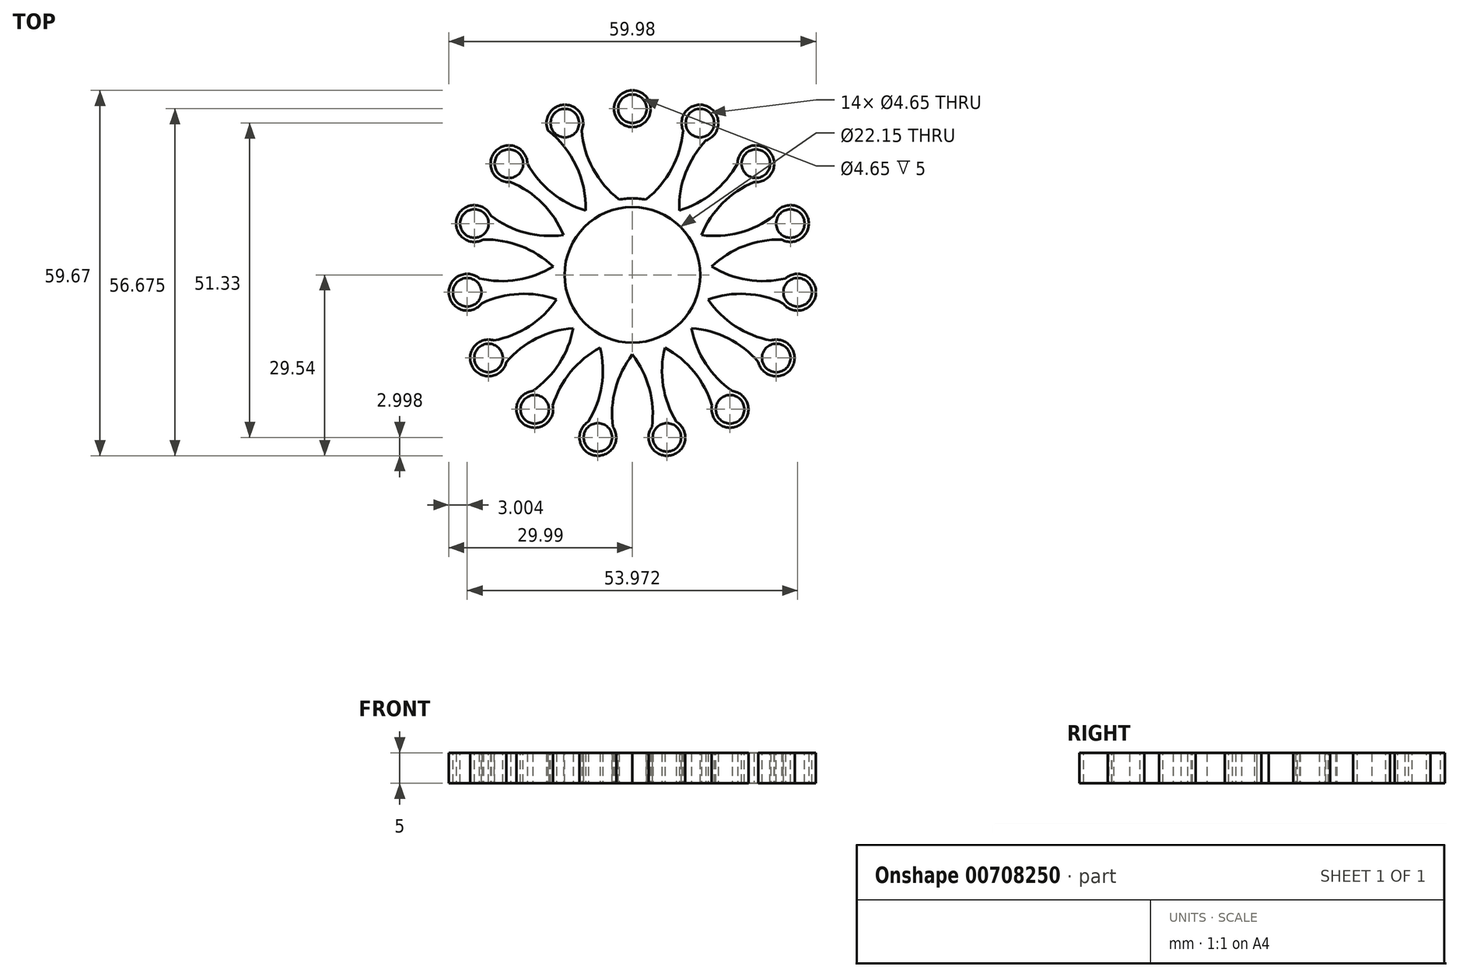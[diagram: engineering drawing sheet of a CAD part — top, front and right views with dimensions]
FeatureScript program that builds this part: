
annotation { "Feature Type Name" : "Feature", "Feature Type Description" : "" }
export const myFeature = defineFeature(function(context is Context, id is Id, definition is map)
    precondition{}
    {
        {
            var Q0;
            Q0=qCreatedBy(makeId("Top.planeOp"),FACE);
            var sketch = newSketch(context, id + "F0", { "sketchPlane" : qUnion([Q0])});
            skCircle(sketch, "E0", {"center": v(0, 0) * mm, "radius": 12.5 * mm});
            skCircle(sketch, "E1", {"center": v(0, 27.13) * mm, "radius": 3 * mm});
            skLineSegment(sketch, "E2", {"start": v(-3, 12.13) * mm, "end": v(3, 12.13) * mm});
            skArc(sketch, "E3", {"start": v(-3, 12.13) * mm, "mid": v(-1.13, 19.63) * mm, "end": v(-3, 27.13) * mm});
            skArc(sketch, "E4", {"start": v(3, 27.13) * mm, "mid": v(1.13, 19.63) * mm, "end": v(3, 12.13) * mm});
            skArc(sketch, "E5.1.0", {"start": v(-8.3, 26) * mm, "mid": v(-6.95, 18.4) * mm, "end": v(-2.2, 12.3) * mm});
            skArc(sketch, "E5.1.2", {"start": v(-7.68, 9.87) * mm, "mid": v(-9.02, 17.48) * mm, "end": v(-13.78, 23.57) * mm});
            skCircle(sketch, "E5.1.3", {"center": v(-11.04, 24.79) * mm, "radius": 3 * mm});
            skLineSegment(sketch, "E5.1.4", {"start": v(-7.68, 9.87) * mm, "end": v(-2.2, 12.3) * mm});
            skArc(sketch, "E5.2.0", {"start": v(-18.16, 20.39) * mm, "mid": v(-13.83, 13.98) * mm, "end": v(-7.01, 10.35) * mm});
            skArc(sketch, "E5.2.2", {"start": v(-11.03, 5.9) * mm, "mid": v(-15.35, 12.3) * mm, "end": v(-22.17, 15.93) * mm});
            skCircle(sketch, "E5.2.3", {"center": v(-20.16, 18.16) * mm, "radius": 3 * mm});
            skLineSegment(sketch, "E5.2.4", {"start": v(-11.03, 5.9) * mm, "end": v(-7.01, 10.35) * mm});
            skArc(sketch, "E6.6.3.0", {"start": v(-12.47, 0.9) * mm, "mid": v(-19.02, 4.99) * mm, "end": v(-26.73, 5.53) * mm});
            skArc(sketch, "E6.7.3.0", {"start": v(-24.88, 11.24) * mm, "mid": v(-18.32, 7.15) * mm, "end": v(-10.61, 6.6) * mm});
            skCircle(sketch, "E6.10.3.0", {"center": v(-25.8, 8.39) * mm, "radius": 3 * mm});
            skLineSegment(sketch, "E6.12.3.0", {"start": v(-12.47, 0.9) * mm, "end": v(-10.61, 6.6) * mm});
            skArc(sketch, "E6.6.4.0", {"start": v(-11.75, -4.25) * mm, "mid": v(-19.4, -3.18) * mm, "end": v(-26.67, -5.82) * mm});
            skArc(sketch, "E6.7.4.0", {"start": v(-27.3, 0.15) * mm, "mid": v(-19.65, -0.93) * mm, "end": v(-12.38, 1.72) * mm});
            skCircle(sketch, "E6.10.4.0", {"center": v(-26.99, -2.84) * mm, "radius": 3 * mm});
            skLineSegment(sketch, "E6.12.4.0", {"start": v(-11.75, -4.25) * mm, "end": v(-12.38, 1.72) * mm});
            skArc(sketch, "E6.6.5.0", {"start": v(-9, -8.67) * mm, "mid": v(-16.44, -10.8) * mm, "end": v(-22, -16.17) * mm});
            skArc(sketch, "E6.7.5.0", {"start": v(-25, -10.97) * mm, "mid": v(-17.57, -8.84) * mm, "end": v(-12, -3.47) * mm});
            skCircle(sketch, "E6.10.5.0", {"center": v(-23.5, -13.57) * mm, "radius": 3 * mm});
            skLineSegment(sketch, "E6.12.5.0", {"start": v(-9, -8.67) * mm, "end": v(-12, -3.47) * mm});
            skArc(sketch, "E6.6.6.0", {"start": v(-4.7, -11.58) * mm, "mid": v(-10.62, -16.55) * mm, "end": v(-13.52, -23.72) * mm});
            skArc(sketch, "E6.7.6.0", {"start": v(-18.38, -20.19) * mm, "mid": v(-12.46, -15.22) * mm, "end": v(-9.56, -8.05) * mm});
            skCircle(sketch, "E6.10.6.0", {"center": v(-15.95, -21.95) * mm, "radius": 3 * mm});
            skLineSegment(sketch, "E6.12.6.0", {"start": v(-4.7, -11.58) * mm, "end": v(-9.56, -8.05) * mm});
            skArc(sketch, "E7.6.7.0", {"start": v(0.41, -12.5) * mm, "mid": v(-2.97, -19.44) * mm, "end": v(-2.7, -27.17) * mm});
            skArc(sketch, "E7.7.7.0", {"start": v(-8.58, -25.92) * mm, "mid": v(-5.2, -18.97) * mm, "end": v(-5.46, -11.25) * mm});
            skCircle(sketch, "E7.10.7.0", {"center": v(-5.64, -26.54) * mm, "radius": 3 * mm});
            skLineSegment(sketch, "E7.12.7.0", {"start": v(0.41, -12.5) * mm, "end": v(-5.46, -11.25) * mm});
            skArc(sketch, "E7.6.8.0", {"start": v(5.46, -11.25) * mm, "mid": v(5.2, -18.97) * mm, "end": v(8.58, -25.92) * mm});
            skArc(sketch, "E7.7.8.0", {"start": v(2.7, -27.17) * mm, "mid": v(2.97, -19.44) * mm, "end": v(-0.41, -12.5) * mm});
            skCircle(sketch, "E7.10.8.0", {"center": v(5.64, -26.54) * mm, "radius": 3 * mm});
            skLineSegment(sketch, "E7.12.8.0", {"start": v(5.46, -11.25) * mm, "end": v(-0.41, -12.5) * mm});
            skArc(sketch, "E7.6.9.0", {"start": v(9.56, -8.05) * mm, "mid": v(12.46, -15.22) * mm, "end": v(18.38, -20.19) * mm});
            skArc(sketch, "E7.7.9.0", {"start": v(13.52, -23.72) * mm, "mid": v(10.62, -16.55) * mm, "end": v(4.7, -11.58) * mm});
            skCircle(sketch, "E7.10.9.0", {"center": v(15.95, -21.95) * mm, "radius": 3 * mm});
            skLineSegment(sketch, "E7.12.9.0", {"start": v(9.56, -8.05) * mm, "end": v(4.7, -11.58) * mm});
            skArc(sketch, "E7.6.10.0", {"start": v(12, -3.47) * mm, "mid": v(17.57, -8.84) * mm, "end": v(25, -10.97) * mm});
            skArc(sketch, "E7.7.10.0", {"start": v(22, -16.17) * mm, "mid": v(16.44, -10.8) * mm, "end": v(9, -8.67) * mm});
            skCircle(sketch, "E7.10.10.0", {"center": v(23.5, -13.57) * mm, "radius": 3 * mm});
            skLineSegment(sketch, "E7.12.10.0", {"start": v(12, -3.47) * mm, "end": v(9, -8.67) * mm});
            skArc(sketch, "E7.6.11.0", {"start": v(12.38, 1.72) * mm, "mid": v(19.65, -0.93) * mm, "end": v(27.3, 0.15) * mm});
            skArc(sketch, "E7.7.11.0", {"start": v(26.67, -5.82) * mm, "mid": v(19.4, -3.18) * mm, "end": v(11.75, -4.25) * mm});
            skCircle(sketch, "E7.10.11.0", {"center": v(26.99, -2.84) * mm, "radius": 3 * mm});
            skLineSegment(sketch, "E7.12.11.0", {"start": v(12.38, 1.72) * mm, "end": v(11.75, -4.25) * mm});
            skArc(sketch, "E7.6.12.0", {"start": v(10.61, 6.6) * mm, "mid": v(18.32, 7.15) * mm, "end": v(24.88, 11.24) * mm});
            skArc(sketch, "E7.7.12.0", {"start": v(26.73, 5.53) * mm, "mid": v(19.02, 4.99) * mm, "end": v(12.47, 0.9) * mm});
            skCircle(sketch, "E7.10.12.0", {"center": v(25.8, 8.39) * mm, "radius": 3 * mm});
            skLineSegment(sketch, "E7.12.12.0", {"start": v(10.61, 6.6) * mm, "end": v(12.47, 0.9) * mm});
            skArc(sketch, "E7.6.13.0", {"start": v(7.01, 10.35) * mm, "mid": v(13.83, 13.98) * mm, "end": v(18.16, 20.39) * mm});
            skArc(sketch, "E7.7.13.0", {"start": v(22.17, 15.93) * mm, "mid": v(15.35, 12.3) * mm, "end": v(11.03, 5.9) * mm});
            skCircle(sketch, "E7.10.13.0", {"center": v(20.16, 18.16) * mm, "radius": 3 * mm});
            skLineSegment(sketch, "E7.12.13.0", {"start": v(7.01, 10.35) * mm, "end": v(11.03, 5.9) * mm});
            skArc(sketch, "E7.6.14.0", {"start": v(2.2, 12.3) * mm, "mid": v(6.95, 18.4) * mm, "end": v(8.3, 26) * mm});
            skArc(sketch, "E7.7.14.0", {"start": v(13.78, 23.57) * mm, "mid": v(9.02, 17.48) * mm, "end": v(7.68, 9.87) * mm});
            skCircle(sketch, "E7.10.14.0", {"center": v(11.04, 24.79) * mm, "radius": 3 * mm});
            skLineSegment(sketch, "E7.12.14.0", {"start": v(2.2, 12.3) * mm, "end": v(7.68, 9.87) * mm});
            skSolve(sketch);
        }
        {
            var Q0;
            {var subQ0=sQuery(id+"F0.wireOp",EDGE,"E7.6.14.0");var subQ1=sQuery(id+"F0.wireOp",EDGE,"E4");var subQ2=makeQuery(id+"F0.imprint","INTERSECT",VERTEX,{"derivedFrom":[subQ1,subQ0]});Q0=makeQuery(id+"F0.imprint","IMPRINT",FACE,{"disambiguationData":[TD([[makeQuery(id+"F0.imprint","IMPRINT",EDGE,{"disambiguationData":[TD([[subQ2,-1.0]])],"derivedFrom":subQ0}),-1.0]])]});}
            var Q1;
            {var subQ0=sQuery(id+"F0.wireOp",EDGE,"E6.10.5.0");var subQ1=sQuery(id+"F0.wireOp",EDGE,"E6.6.5.0");var subQ2=makeQuery(id+"F0.imprint","INTERSECT",VERTEX,{"disambiguationData":[OD(0.0)],"derivedFrom":[subQ1,subQ0]});Q1=makeQuery(id+"F0.imprint","IMPRINT",FACE,{"disambiguationData":[TD([[makeQuery(id+"F0.imprint","IMPRINT",EDGE,{"disambiguationData":[TD([[subQ2,1.0]])],"derivedFrom":subQ1}),-1.0]])]});}
            var Q2;
            {var subQ1=sQuery(id+"F0.wireOp",EDGE,"E6.6.6.0");var subQ9=sQuery(id+"F0.wireOp",EDGE,"E7.7.7.0");var subQ11=makeQuery(id+"F0.imprint","INTERSECT",VERTEX,{"derivedFrom":[subQ1,subQ9]});Q2=makeQuery(id+"F0.imprint","IMPRINT",FACE,{"disambiguationData":[TD([[makeQuery(id+"F0.imprint","IMPRINT",EDGE,{"disambiguationData":[TD([[subQ11,-1.0]])],"derivedFrom":subQ1}),-1.0]])]});}
            var Q3;
            {var subQ0=sQuery(id+"F0.wireOp",EDGE,"E5.2.3");var subQ1=sQuery(id+"F0.wireOp",EDGE,"E5.2.0");var subQ2=makeQuery(id+"F0.imprint","INTERSECT",VERTEX,{"disambiguationData":[OD(0.0)],"derivedFrom":[subQ1,subQ0]});Q3=makeQuery(id+"F0.imprint","IMPRINT",FACE,{"disambiguationData":[TD([[makeQuery(id+"F0.imprint","IMPRINT",EDGE,{"disambiguationData":[TD([[subQ2,-1.0]])],"derivedFrom":subQ1}),-1.0]])]});}
            var Q4;
            {var subQ0=sQuery(id+"F0.wireOp",EDGE,"E7.10.8.0");var subQ1=sQuery(id+"F0.wireOp",EDGE,"E7.6.8.0");var subQ2=makeQuery(id+"F0.imprint","INTERSECT",VERTEX,{"disambiguationData":[OD(0.0)],"derivedFrom":[subQ1,subQ0]});Q4=makeQuery(id+"F0.imprint","IMPRINT",FACE,{"disambiguationData":[TD([[makeQuery(id+"F0.imprint","IMPRINT",EDGE,{"disambiguationData":[TD([[subQ2,1.0]])],"derivedFrom":subQ1}),-1.0]])]});}
            var Q5;
            {var subQ1=sQuery(id+"F0.wireOp",EDGE,"E7.6.10.0");var subQ9=sQuery(id+"F0.wireOp",EDGE,"E7.7.11.0");var subQ11=makeQuery(id+"F0.imprint","INTERSECT",VERTEX,{"derivedFrom":[subQ1,subQ9]});Q5=makeQuery(id+"F0.imprint","IMPRINT",FACE,{"disambiguationData":[TD([[makeQuery(id+"F0.imprint","IMPRINT",EDGE,{"disambiguationData":[TD([[subQ11,-1.0]])],"derivedFrom":subQ1}),-1.0]])]});}
            var Q6;
            {var subQ0=sQuery(id+"F0.wireOp",EDGE,"E5.1.3");var subQ1=sQuery(id+"F0.wireOp",EDGE,"E5.1.0");var subQ2=makeQuery(id+"F0.imprint","INTERSECT",VERTEX,{"disambiguationData":[OD(0.0)],"derivedFrom":[subQ1,subQ0]});Q6=makeQuery(id+"F0.imprint","IMPRINT",FACE,{"disambiguationData":[TD([[makeQuery(id+"F0.imprint","IMPRINT",EDGE,{"disambiguationData":[TD([[subQ2,-1.0]])],"derivedFrom":subQ1}),-1.0]])]});}
            var Q7;
            {var subQ1=sQuery(id+"F0.wireOp",EDGE,"E7.6.9.0");var subQ9=sQuery(id+"F0.wireOp",EDGE,"E7.7.10.0");var subQ11=makeQuery(id+"F0.imprint","INTERSECT",VERTEX,{"derivedFrom":[subQ1,subQ9]});Q7=makeQuery(id+"F0.imprint","IMPRINT",FACE,{"disambiguationData":[TD([[makeQuery(id+"F0.imprint","IMPRINT",EDGE,{"disambiguationData":[TD([[subQ11,-1.0]])],"derivedFrom":subQ1}),-1.0]])]});}
            var Q8;
            {var subQ0=sQuery(id+"F0.wireOp",EDGE,"E7.10.12.0");var subQ1=sQuery(id+"F0.wireOp",EDGE,"E7.6.12.0");var subQ2=makeQuery(id+"F0.imprint","INTERSECT",VERTEX,{"disambiguationData":[OD(0.0)],"derivedFrom":[subQ1,subQ0]});Q8=makeQuery(id+"F0.imprint","IMPRINT",FACE,{"disambiguationData":[TD([[makeQuery(id+"F0.imprint","IMPRINT",EDGE,{"disambiguationData":[TD([[subQ2,1.0]])],"derivedFrom":subQ1}),-1.0]])]});}
            var Q9;
            {var subQ1=sQuery(id+"F0.wireOp",EDGE,"E7.6.12.0");var subQ7=sQuery(id+"F0.wireOp",EDGE,"E7.7.13.0");var subQ8=makeQuery(id+"F0.imprint","INTERSECT",VERTEX,{"derivedFrom":[subQ1,subQ7]});Q9=makeQuery(id+"F0.imprint","IMPRINT",FACE,{"disambiguationData":[TD([[makeQuery(id+"F0.imprint","IMPRINT",EDGE,{"disambiguationData":[TD([[subQ8,-1.0]])],"derivedFrom":subQ1}),-1.0]])]});}
            var Q10;
            {var subQ1=sQuery(id+"F0.wireOp",EDGE,"E7.6.7.0");var subQ9=sQuery(id+"F0.wireOp",EDGE,"E7.7.8.0");var subQ11=makeQuery(id+"F0.imprint","INTERSECT",VERTEX,{"derivedFrom":[subQ1,subQ9]});Q10=makeQuery(id+"F0.imprint","IMPRINT",FACE,{"disambiguationData":[TD([[makeQuery(id+"F0.imprint","IMPRINT",EDGE,{"disambiguationData":[TD([[subQ11,-1.0]])],"derivedFrom":subQ1}),-1.0]])]});}
            var Q11;
            {var subQ0=sQuery(id+"F0.wireOp",EDGE,"E6.10.6.0");var subQ1=sQuery(id+"F0.wireOp",EDGE,"E6.6.6.0");var subQ2=makeQuery(id+"F0.imprint","INTERSECT",VERTEX,{"disambiguationData":[OD(0.0)],"derivedFrom":[subQ1,subQ0]});Q11=makeQuery(id+"F0.imprint","IMPRINT",FACE,{"disambiguationData":[TD([[makeQuery(id+"F0.imprint","IMPRINT",EDGE,{"disambiguationData":[TD([[subQ2,1.0]])],"derivedFrom":subQ1}),-1.0]])]});}
            var Q12;
            {var subQ1=sQuery(id+"F0.wireOp",EDGE,"E6.6.4.0");var subQ9=sQuery(id+"F0.wireOp",EDGE,"E6.7.5.0");var subQ11=makeQuery(id+"F0.imprint","INTERSECT",VERTEX,{"derivedFrom":[subQ1,subQ9]});Q12=makeQuery(id+"F0.imprint","IMPRINT",FACE,{"disambiguationData":[TD([[makeQuery(id+"F0.imprint","IMPRINT",EDGE,{"disambiguationData":[TD([[subQ11,-1.0]])],"derivedFrom":subQ1}),-1.0]])]});}
            var Q13;
            {var subQ1=sQuery(id+"F0.wireOp",EDGE,"E5.2.0");var subQ8=sQuery(id+"F0.wireOp",EDGE,"E5.1.2");var subQ11=makeQuery(id+"F0.imprint","INTERSECT",VERTEX,{"derivedFrom":[subQ8,subQ1]});Q13=makeQuery(id+"F0.imprint","IMPRINT",FACE,{"disambiguationData":[TD([[makeQuery(id+"F0.imprint","IMPRINT",EDGE,{"disambiguationData":[TD([[subQ11,1.0]])],"derivedFrom":subQ1}),-1.0]])]});}
            var Q14;
            {var subQ15=sQuery(id+"F0.wireOp",EDGE,"E5.1.4");var subQ16=sQuery(id+"F0.wireOp",EDGE,"E2");var subQ17=makeQuery(id+"F0.imprint","INTERSECT",VERTEX,{"derivedFrom":[subQ16,subQ15]});Q14=makeQuery(id+"F0.imprint","IMPRINT",FACE,{"disambiguationData":[TD([[makeQuery(id+"F0.imprint","IMPRINT",EDGE,{"disambiguationData":[TD([[subQ17,-1.0]])],"derivedFrom":subQ16}),-1.0]])]});}
            var Q15;
            {var subQ1=sQuery(id+"F0.wireOp",EDGE,"E6.6.5.0");var subQ9=sQuery(id+"F0.wireOp",EDGE,"E6.7.6.0");var subQ11=makeQuery(id+"F0.imprint","INTERSECT",VERTEX,{"derivedFrom":[subQ1,subQ9]});Q15=makeQuery(id+"F0.imprint","IMPRINT",FACE,{"disambiguationData":[TD([[makeQuery(id+"F0.imprint","IMPRINT",EDGE,{"disambiguationData":[TD([[subQ11,-1.0]])],"derivedFrom":subQ1}),-1.0]])]});}
            var Q16;
            {var subQ1=sQuery(id+"F0.wireOp",EDGE,"E7.6.13.0");var subQ7=sQuery(id+"F0.wireOp",EDGE,"E7.7.14.0");var subQ10=makeQuery(id+"F0.imprint","INTERSECT",VERTEX,{"derivedFrom":[subQ1,subQ7]});Q16=makeQuery(id+"F0.imprint","IMPRINT",FACE,{"disambiguationData":[TD([[makeQuery(id+"F0.imprint","IMPRINT",EDGE,{"disambiguationData":[TD([[subQ10,-1.0]])],"derivedFrom":subQ1}),-1.0]])]});}
            var Q17;
            {var subQ0=sQuery(id+"F0.wireOp",EDGE,"E7.10.14.0");var subQ1=sQuery(id+"F0.wireOp",EDGE,"E7.6.14.0");var subQ2=makeQuery(id+"F0.imprint","INTERSECT",VERTEX,{"disambiguationData":[OD(0.0)],"derivedFrom":[subQ1,subQ0]});Q17=makeQuery(id+"F0.imprint","IMPRINT",FACE,{"disambiguationData":[TD([[makeQuery(id+"F0.imprint","IMPRINT",EDGE,{"disambiguationData":[TD([[subQ2,1.0]])],"derivedFrom":subQ1}),-1.0]])]});}
            var Q18;
            {var subQ1=sQuery(id+"F0.wireOp",EDGE,"E7.6.8.0");var subQ9=sQuery(id+"F0.wireOp",EDGE,"E7.7.9.0");var subQ11=makeQuery(id+"F0.imprint","INTERSECT",VERTEX,{"derivedFrom":[subQ1,subQ9]});Q18=makeQuery(id+"F0.imprint","IMPRINT",FACE,{"disambiguationData":[TD([[makeQuery(id+"F0.imprint","IMPRINT",EDGE,{"disambiguationData":[TD([[subQ11,-1.0]])],"derivedFrom":subQ1}),-1.0]])]});}
            var Q19;
            {var subQ1=sQuery(id+"F0.wireOp",EDGE,"E7.6.11.0");var subQ7=sQuery(id+"F0.wireOp",EDGE,"E7.7.12.0");var subQ8=makeQuery(id+"F0.imprint","INTERSECT",VERTEX,{"derivedFrom":[subQ1,subQ7]});Q19=makeQuery(id+"F0.imprint","IMPRINT",FACE,{"disambiguationData":[TD([[makeQuery(id+"F0.imprint","IMPRINT",EDGE,{"disambiguationData":[TD([[subQ8,-1.0]])],"derivedFrom":subQ1}),-1.0]])]});}
            var Q20;
            {var subQ0=sQuery(id+"F0.wireOp",EDGE,"E3");var subQ1=sQuery(id+"F0.wireOp",EDGE,"E1");var subQ2=makeQuery(id+"F0.imprint","INTERSECT",VERTEX,{"disambiguationData":[OD(0.0)],"derivedFrom":[subQ1,subQ0]});Q20=makeQuery(id+"F0.imprint","IMPRINT",FACE,{"disambiguationData":[TD([[makeQuery(id+"F0.imprint","IMPRINT",EDGE,{"disambiguationData":[TD([[subQ2,1.0]])],"derivedFrom":subQ1}),1.0]])]});}
            var Q21;
            {var subQ0=sQuery(id+"F0.wireOp",EDGE,"E6.10.3.0");var subQ1=sQuery(id+"F0.wireOp",EDGE,"E6.6.3.0");var subQ2=makeQuery(id+"F0.imprint","INTERSECT",VERTEX,{"disambiguationData":[OD(0.0)],"derivedFrom":[subQ1,subQ0]});Q21=makeQuery(id+"F0.imprint","IMPRINT",FACE,{"disambiguationData":[TD([[makeQuery(id+"F0.imprint","IMPRINT",EDGE,{"disambiguationData":[TD([[subQ2,1.0]])],"derivedFrom":subQ1}),-1.0]])]});}
            var Q22;
            {var subQ0=sQuery(id+"F0.wireOp",EDGE,"E7.10.11.0");var subQ1=sQuery(id+"F0.wireOp",EDGE,"E7.6.11.0");var subQ2=makeQuery(id+"F0.imprint","INTERSECT",VERTEX,{"disambiguationData":[OD(0.0)],"derivedFrom":[subQ1,subQ0]});Q22=makeQuery(id+"F0.imprint","IMPRINT",FACE,{"disambiguationData":[TD([[makeQuery(id+"F0.imprint","IMPRINT",EDGE,{"disambiguationData":[TD([[subQ2,1.0]])],"derivedFrom":subQ1}),-1.0]])]});}
            var Q23;
            {var subQ0=sQuery(id+"F0.wireOp",EDGE,"E6.10.4.0");var subQ1=sQuery(id+"F0.wireOp",EDGE,"E6.6.4.0");var subQ2=makeQuery(id+"F0.imprint","INTERSECT",VERTEX,{"disambiguationData":[OD(0.0)],"derivedFrom":[subQ1,subQ0]});Q23=makeQuery(id+"F0.imprint","IMPRINT",FACE,{"disambiguationData":[TD([[makeQuery(id+"F0.imprint","IMPRINT",EDGE,{"disambiguationData":[TD([[subQ2,1.0]])],"derivedFrom":subQ1}),-1.0]])]});}
            var Q24;
            {var subQ3=sQuery(id+"F0.wireOp",EDGE,"E3");var subQ8=sQuery(id+"F0.wireOp",EDGE,"E1");var subQ11=makeQuery(id+"F0.imprint","INTERSECT",VERTEX,{"disambiguationData":[OD(1.0)],"derivedFrom":[subQ8,subQ3]});Q24=makeQuery(id+"F0.imprint","IMPRINT",FACE,{"disambiguationData":[TD([[makeQuery(id+"F0.imprint","IMPRINT",EDGE,{"disambiguationData":[TD([[subQ11,-1.0]])],"derivedFrom":subQ8}),-1.0]])]});}
            var Q25;
            {var subQ0=sQuery(id+"F0.wireOp",EDGE,"E7.10.9.0");var subQ1=sQuery(id+"F0.wireOp",EDGE,"E7.6.9.0");var subQ2=makeQuery(id+"F0.imprint","INTERSECT",VERTEX,{"disambiguationData":[OD(0.0)],"derivedFrom":[subQ1,subQ0]});Q25=makeQuery(id+"F0.imprint","IMPRINT",FACE,{"disambiguationData":[TD([[makeQuery(id+"F0.imprint","IMPRINT",EDGE,{"disambiguationData":[TD([[subQ2,1.0]])],"derivedFrom":subQ1}),-1.0]])]});}
            var Q26;
            {var subQ0=sQuery(id+"F0.wireOp",EDGE,"E7.10.13.0");var subQ1=sQuery(id+"F0.wireOp",EDGE,"E7.6.13.0");var subQ2=makeQuery(id+"F0.imprint","INTERSECT",VERTEX,{"disambiguationData":[OD(0.0)],"derivedFrom":[subQ1,subQ0]});Q26=makeQuery(id+"F0.imprint","IMPRINT",FACE,{"disambiguationData":[TD([[makeQuery(id+"F0.imprint","IMPRINT",EDGE,{"disambiguationData":[TD([[subQ2,1.0]])],"derivedFrom":subQ1}),-1.0]])]});}
            var Q27;
            {var subQ1=sQuery(id+"F0.wireOp",EDGE,"E5.1.0");var subQ5=sQuery(id+"F0.wireOp",EDGE,"E3");var subQ6=makeQuery(id+"F0.imprint","INTERSECT",VERTEX,{"derivedFrom":[subQ5,subQ1]});Q27=makeQuery(id+"F0.imprint","IMPRINT",FACE,{"disambiguationData":[TD([[makeQuery(id+"F0.imprint","IMPRINT",EDGE,{"disambiguationData":[TD([[subQ6,1.0]])],"derivedFrom":subQ1}),-1.0]])]});}
            var Q28;
            {var subQ0=sQuery(id+"F0.wireOp",EDGE,"E7.10.7.0");var subQ1=sQuery(id+"F0.wireOp",EDGE,"E7.6.7.0");var subQ2=makeQuery(id+"F0.imprint","INTERSECT",VERTEX,{"disambiguationData":[OD(0.0)],"derivedFrom":[subQ1,subQ0]});Q28=makeQuery(id+"F0.imprint","IMPRINT",FACE,{"disambiguationData":[TD([[makeQuery(id+"F0.imprint","IMPRINT",EDGE,{"disambiguationData":[TD([[subQ2,1.0]])],"derivedFrom":subQ1}),-1.0]])]});}
            var Q29;
            {var subQ1=sQuery(id+"F0.wireOp",EDGE,"E6.6.3.0");var subQ9=sQuery(id+"F0.wireOp",EDGE,"E6.7.4.0");var subQ11=makeQuery(id+"F0.imprint","INTERSECT",VERTEX,{"derivedFrom":[subQ1,subQ9]});Q29=makeQuery(id+"F0.imprint","IMPRINT",FACE,{"disambiguationData":[TD([[makeQuery(id+"F0.imprint","IMPRINT",EDGE,{"disambiguationData":[TD([[subQ11,-1.0]])],"derivedFrom":subQ1}),-1.0]])]});}
            var Q30;
            {var subQ0=sQuery(id+"F0.wireOp",EDGE,"E7.10.10.0");var subQ1=sQuery(id+"F0.wireOp",EDGE,"E7.6.10.0");var subQ2=makeQuery(id+"F0.imprint","INTERSECT",VERTEX,{"disambiguationData":[OD(0.0)],"derivedFrom":[subQ1,subQ0]});Q30=makeQuery(id+"F0.imprint","IMPRINT",FACE,{"disambiguationData":[TD([[makeQuery(id+"F0.imprint","IMPRINT",EDGE,{"disambiguationData":[TD([[subQ2,1.0]])],"derivedFrom":subQ1}),-1.0]])]});}
            var Q31;
            {var subQ1=sQuery(id+"F0.wireOp",EDGE,"E6.12.6.0");var subQ3=sQuery(id+"F0.wireOp",EDGE,"E7.12.7.0");var subQ4=makeQuery(id+"F0.imprint","INTERSECT",VERTEX,{"derivedFrom":[subQ1,subQ3]});Q31=makeQuery(id+"F0.imprint","IMPRINT",FACE,{"disambiguationData":[TD([[makeQuery(id+"F0.imprint","IMPRINT",EDGE,{"disambiguationData":[TD([[subQ4,1.0]])],"derivedFrom":subQ3}),1.0]])]});}
            var Q32;
            {var subQ0=sQuery(id+"F0.wireOp",EDGE,"E7.10.11.0");var subQ1=sQuery(id+"F0.wireOp",EDGE,"E7.6.11.0");var subQ2=makeQuery(id+"F0.imprint","INTERSECT",VERTEX,{"disambiguationData":[OD(0.0)],"derivedFrom":[subQ1,subQ0]});Q32=makeQuery(id+"F0.imprint","IMPRINT",FACE,{"disambiguationData":[TD([[makeQuery(id+"F0.imprint","IMPRINT",EDGE,{"disambiguationData":[TD([[subQ2,1.0]])],"derivedFrom":subQ1}),1.0]])]});}
            var Q33;
            {var subQ0=sQuery(id+"F0.wireOp",EDGE,"E7.10.8.0");var subQ1=sQuery(id+"F0.wireOp",EDGE,"E7.6.8.0");var subQ2=makeQuery(id+"F0.imprint","INTERSECT",VERTEX,{"disambiguationData":[OD(0.0)],"derivedFrom":[subQ1,subQ0]});Q33=makeQuery(id+"F0.imprint","IMPRINT",FACE,{"disambiguationData":[TD([[makeQuery(id+"F0.imprint","IMPRINT",EDGE,{"disambiguationData":[TD([[subQ2,1.0]])],"derivedFrom":subQ1}),1.0]])]});}
            var Q34;
            {var subQ0=sQuery(id+"F0.wireOp",EDGE,"E5.2.3");var subQ1=sQuery(id+"F0.wireOp",EDGE,"E5.2.0");var subQ2=makeQuery(id+"F0.imprint","INTERSECT",VERTEX,{"disambiguationData":[OD(0.0)],"derivedFrom":[subQ1,subQ0]});Q34=makeQuery(id+"F0.imprint","IMPRINT",FACE,{"disambiguationData":[TD([[makeQuery(id+"F0.imprint","IMPRINT",EDGE,{"disambiguationData":[TD([[subQ2,-1.0]])],"derivedFrom":subQ1}),1.0]])]});}
            var Q35;
            {var subQ0=sQuery(id+"F0.wireOp",EDGE,"E7.10.7.0");var subQ1=sQuery(id+"F0.wireOp",EDGE,"E7.6.7.0");var subQ2=makeQuery(id+"F0.imprint","INTERSECT",VERTEX,{"disambiguationData":[OD(0.0)],"derivedFrom":[subQ1,subQ0]});Q35=makeQuery(id+"F0.imprint","IMPRINT",FACE,{"disambiguationData":[TD([[makeQuery(id+"F0.imprint","IMPRINT",EDGE,{"disambiguationData":[TD([[subQ2,1.0]])],"derivedFrom":subQ1}),1.0]])]});}
            var Q36;
            {var subQ0=sQuery(id+"F0.wireOp",EDGE,"E6.10.6.0");var subQ1=sQuery(id+"F0.wireOp",EDGE,"E6.6.6.0");var subQ2=makeQuery(id+"F0.imprint","INTERSECT",VERTEX,{"disambiguationData":[OD(0.0)],"derivedFrom":[subQ1,subQ0]});Q36=makeQuery(id+"F0.imprint","IMPRINT",FACE,{"disambiguationData":[TD([[makeQuery(id+"F0.imprint","IMPRINT",EDGE,{"disambiguationData":[TD([[subQ2,1.0]])],"derivedFrom":subQ1}),1.0]])]});}
            var Q37;
            {var subQ0=sQuery(id+"F0.wireOp",EDGE,"E3");var subQ1=sQuery(id+"F0.wireOp",EDGE,"E1");var subQ2=makeQuery(id+"F0.imprint","INTERSECT",VERTEX,{"disambiguationData":[OD(0.0)],"derivedFrom":[subQ1,subQ0]});Q37=makeQuery(id+"F0.imprint","IMPRINT",FACE,{"disambiguationData":[TD([[makeQuery(id+"F0.imprint","IMPRINT",EDGE,{"disambiguationData":[TD([[subQ2,-1.0]])],"derivedFrom":subQ1}),1.0]])]});}
            var Q38;
            {var subQ0=sQuery(id+"F0.wireOp",EDGE,"E7.10.10.0");var subQ1=sQuery(id+"F0.wireOp",EDGE,"E7.7.10.0");var subQ2=makeQuery(id+"F0.imprint","INTERSECT",VERTEX,{"disambiguationData":[OD(0.0)],"derivedFrom":[subQ1,subQ0]});Q38=makeQuery(id+"F0.imprint","IMPRINT",FACE,{"disambiguationData":[TD([[makeQuery(id+"F0.imprint","IMPRINT",EDGE,{"disambiguationData":[TD([[subQ2,-1.0]])],"derivedFrom":subQ1}),1.0]])]});}
            var Q39;
            {var subQ1=sQuery(id+"F0.wireOp",EDGE,"E7.12.7.0");var subQ3=sQuery(id+"F0.wireOp",EDGE,"E7.12.8.0");var subQ4=makeQuery(id+"F0.imprint","INTERSECT",VERTEX,{"derivedFrom":[subQ1,subQ3]});Q39=makeQuery(id+"F0.imprint","IMPRINT",FACE,{"disambiguationData":[TD([[makeQuery(id+"F0.imprint","IMPRINT",EDGE,{"disambiguationData":[TD([[subQ4,1.0]])],"derivedFrom":subQ3}),1.0]])]});}
            var Q40;
            {var subQ0=sQuery(id+"F0.wireOp",EDGE,"E7.10.12.0");var subQ1=sQuery(id+"F0.wireOp",EDGE,"E7.7.12.0");var subQ2=makeQuery(id+"F0.imprint","INTERSECT",VERTEX,{"disambiguationData":[OD(0.0)],"derivedFrom":[subQ1,subQ0]});Q40=makeQuery(id+"F0.imprint","IMPRINT",FACE,{"disambiguationData":[TD([[makeQuery(id+"F0.imprint","IMPRINT",EDGE,{"disambiguationData":[TD([[subQ2,-1.0]])],"derivedFrom":subQ1}),1.0]])]});}
            var Q41;
            {var subQ0=sQuery(id+"F0.wireOp",EDGE,"E7.10.13.0");var subQ1=sQuery(id+"F0.wireOp",EDGE,"E7.6.13.0");var subQ2=makeQuery(id+"F0.imprint","INTERSECT",VERTEX,{"disambiguationData":[OD(0.0)],"derivedFrom":[subQ1,subQ0]});Q41=makeQuery(id+"F0.imprint","IMPRINT",FACE,{"disambiguationData":[TD([[makeQuery(id+"F0.imprint","IMPRINT",EDGE,{"disambiguationData":[TD([[subQ2,1.0]])],"derivedFrom":subQ1}),1.0]])]});}
            var Q42;
            {var subQ0=sQuery(id+"F0.wireOp",EDGE,"E7.10.13.0");var subQ1=sQuery(id+"F0.wireOp",EDGE,"E7.7.13.0");var subQ2=makeQuery(id+"F0.imprint","INTERSECT",VERTEX,{"disambiguationData":[OD(0.0)],"derivedFrom":[subQ1,subQ0]});Q42=makeQuery(id+"F0.imprint","IMPRINT",FACE,{"disambiguationData":[TD([[makeQuery(id+"F0.imprint","IMPRINT",EDGE,{"disambiguationData":[TD([[subQ2,-1.0]])],"derivedFrom":subQ1}),1.0]])]});}
            var Q43;
            {var subQ0=sQuery(id+"F0.wireOp",EDGE,"E5.2.3");var subQ1=sQuery(id+"F0.wireOp",EDGE,"E5.2.2");var subQ2=makeQuery(id+"F0.imprint","INTERSECT",VERTEX,{"disambiguationData":[OD(0.0)],"derivedFrom":[subQ1,subQ0]});Q43=makeQuery(id+"F0.imprint","IMPRINT",FACE,{"disambiguationData":[TD([[makeQuery(id+"F0.imprint","IMPRINT",EDGE,{"disambiguationData":[TD([[subQ2,1.0]])],"derivedFrom":subQ1}),1.0]])]});}
            var Q44;
            {var subQ0=sQuery(id+"F0.wireOp",EDGE,"E7.10.14.0");var subQ1=sQuery(id+"F0.wireOp",EDGE,"E7.7.14.0");var subQ2=makeQuery(id+"F0.imprint","INTERSECT",VERTEX,{"disambiguationData":[OD(0.0)],"derivedFrom":[subQ1,subQ0]});Q44=makeQuery(id+"F0.imprint","IMPRINT",FACE,{"disambiguationData":[TD([[makeQuery(id+"F0.imprint","IMPRINT",EDGE,{"disambiguationData":[TD([[subQ2,-1.0]])],"derivedFrom":subQ1}),1.0]])]});}
            var Q45;
            {var subQ0=sQuery(id+"F0.wireOp",EDGE,"E6.10.4.0");var subQ1=sQuery(id+"F0.wireOp",EDGE,"E6.7.4.0");var subQ2=makeQuery(id+"F0.imprint","INTERSECT",VERTEX,{"disambiguationData":[OD(0.0)],"derivedFrom":[subQ1,subQ0]});Q45=makeQuery(id+"F0.imprint","IMPRINT",FACE,{"disambiguationData":[TD([[makeQuery(id+"F0.imprint","IMPRINT",EDGE,{"disambiguationData":[TD([[subQ2,-1.0]])],"derivedFrom":subQ1}),1.0]])]});}
            var Q46;
            {var subQ1=sQuery(id+"F0.wireOp",EDGE,"E6.12.5.0");var subQ3=sQuery(id+"F0.wireOp",EDGE,"E6.12.6.0");var subQ4=makeQuery(id+"F0.imprint","INTERSECT",VERTEX,{"derivedFrom":[subQ1,subQ3]});Q46=makeQuery(id+"F0.imprint","IMPRINT",FACE,{"disambiguationData":[TD([[makeQuery(id+"F0.imprint","IMPRINT",EDGE,{"disambiguationData":[TD([[subQ4,1.0]])],"derivedFrom":subQ3}),1.0]])]});}
            var Q47;
            {var subQ1=sQuery(id+"F0.wireOp",EDGE,"E7.12.10.0");var subQ3=sQuery(id+"F0.wireOp",EDGE,"E7.12.11.0");var subQ4=makeQuery(id+"F0.imprint","INTERSECT",VERTEX,{"derivedFrom":[subQ1,subQ3]});Q47=makeQuery(id+"F0.imprint","IMPRINT",FACE,{"disambiguationData":[TD([[makeQuery(id+"F0.imprint","IMPRINT",EDGE,{"disambiguationData":[TD([[subQ4,1.0]])],"derivedFrom":subQ3}),1.0]])]});}
            var Q48;
            {var subQ1=sQuery(id+"F0.wireOp",EDGE,"E7.12.8.0");var subQ3=sQuery(id+"F0.wireOp",EDGE,"E7.12.9.0");var subQ4=makeQuery(id+"F0.imprint","INTERSECT",VERTEX,{"derivedFrom":[subQ1,subQ3]});Q48=makeQuery(id+"F0.imprint","IMPRINT",FACE,{"disambiguationData":[TD([[makeQuery(id+"F0.imprint","IMPRINT",EDGE,{"disambiguationData":[TD([[subQ4,1.0]])],"derivedFrom":subQ3}),1.0]])]});}
            var Q49;
            {var subQ0=sQuery(id+"F0.wireOp",EDGE,"E5.1.3");var subQ1=sQuery(id+"F0.wireOp",EDGE,"E5.1.0");var subQ2=makeQuery(id+"F0.imprint","INTERSECT",VERTEX,{"disambiguationData":[OD(0.0)],"derivedFrom":[subQ1,subQ0]});Q49=makeQuery(id+"F0.imprint","IMPRINT",FACE,{"disambiguationData":[TD([[makeQuery(id+"F0.imprint","IMPRINT",EDGE,{"disambiguationData":[TD([[subQ2,-1.0]])],"derivedFrom":subQ1}),1.0]])]});}
            var Q50;
            {var subQ0=sQuery(id+"F0.wireOp",EDGE,"E7.10.10.0");var subQ1=sQuery(id+"F0.wireOp",EDGE,"E7.6.10.0");var subQ2=makeQuery(id+"F0.imprint","INTERSECT",VERTEX,{"disambiguationData":[OD(0.0)],"derivedFrom":[subQ1,subQ0]});Q50=makeQuery(id+"F0.imprint","IMPRINT",FACE,{"disambiguationData":[TD([[makeQuery(id+"F0.imprint","IMPRINT",EDGE,{"disambiguationData":[TD([[subQ2,1.0]])],"derivedFrom":subQ1}),1.0]])]});}
            var Q51;
            {var subQ0=sQuery(id+"F0.wireOp",EDGE,"E6.10.4.0");var subQ1=sQuery(id+"F0.wireOp",EDGE,"E6.6.4.0");var subQ2=makeQuery(id+"F0.imprint","INTERSECT",VERTEX,{"disambiguationData":[OD(0.0)],"derivedFrom":[subQ1,subQ0]});Q51=makeQuery(id+"F0.imprint","IMPRINT",FACE,{"disambiguationData":[TD([[makeQuery(id+"F0.imprint","IMPRINT",EDGE,{"disambiguationData":[TD([[subQ2,1.0]])],"derivedFrom":subQ1}),1.0]])]});}
            var Q52;
            {var subQ1=sQuery(id+"F0.wireOp",EDGE,"E2");var subQ3=sQuery(id+"F0.wireOp",EDGE,"E7.12.14.0");var subQ4=makeQuery(id+"F0.imprint","INTERSECT",VERTEX,{"derivedFrom":[subQ1,subQ3]});Q52=makeQuery(id+"F0.imprint","IMPRINT",FACE,{"disambiguationData":[TD([[makeQuery(id+"F0.imprint","IMPRINT",EDGE,{"disambiguationData":[TD([[subQ4,-1.0]])],"derivedFrom":subQ3}),1.0]])]});}
            var Q53;
            {var subQ0=sQuery(id+"F0.wireOp",EDGE,"E7.10.14.0");var subQ1=sQuery(id+"F0.wireOp",EDGE,"E7.6.14.0");var subQ2=makeQuery(id+"F0.imprint","INTERSECT",VERTEX,{"disambiguationData":[OD(0.0)],"derivedFrom":[subQ1,subQ0]});Q53=makeQuery(id+"F0.imprint","IMPRINT",FACE,{"disambiguationData":[TD([[makeQuery(id+"F0.imprint","IMPRINT",EDGE,{"disambiguationData":[TD([[subQ2,1.0]])],"derivedFrom":subQ1}),1.0]])]});}
            var Q54;
            {var subQ0=sQuery(id+"F0.wireOp",EDGE,"E7.10.8.0");var subQ1=sQuery(id+"F0.wireOp",EDGE,"E7.7.8.0");var subQ2=makeQuery(id+"F0.imprint","INTERSECT",VERTEX,{"disambiguationData":[OD(0.0)],"derivedFrom":[subQ1,subQ0]});Q54=makeQuery(id+"F0.imprint","IMPRINT",FACE,{"disambiguationData":[TD([[makeQuery(id+"F0.imprint","IMPRINT",EDGE,{"disambiguationData":[TD([[subQ2,-1.0]])],"derivedFrom":subQ1}),1.0]])]});}
            var Q55;
            {var subQ0=sQuery(id+"F0.wireOp",EDGE,"E7.10.9.0");var subQ1=sQuery(id+"F0.wireOp",EDGE,"E7.7.9.0");var subQ2=makeQuery(id+"F0.imprint","INTERSECT",VERTEX,{"disambiguationData":[OD(0.0)],"derivedFrom":[subQ1,subQ0]});Q55=makeQuery(id+"F0.imprint","IMPRINT",FACE,{"disambiguationData":[TD([[makeQuery(id+"F0.imprint","IMPRINT",EDGE,{"disambiguationData":[TD([[subQ2,-1.0]])],"derivedFrom":subQ1}),1.0]])]});}
            var Q56;
            {var subQ0=sQuery(id+"F0.wireOp",EDGE,"E7.10.12.0");var subQ1=sQuery(id+"F0.wireOp",EDGE,"E7.6.12.0");var subQ2=makeQuery(id+"F0.imprint","INTERSECT",VERTEX,{"disambiguationData":[OD(0.0)],"derivedFrom":[subQ1,subQ0]});Q56=makeQuery(id+"F0.imprint","IMPRINT",FACE,{"disambiguationData":[TD([[makeQuery(id+"F0.imprint","IMPRINT",EDGE,{"disambiguationData":[TD([[subQ2,1.0]])],"derivedFrom":subQ1}),1.0]])]});}
            var Q57;
            {var subQ0=sQuery(id+"F0.wireOp",EDGE,"E6.10.3.0");var subQ1=sQuery(id+"F0.wireOp",EDGE,"E6.6.3.0");var subQ2=makeQuery(id+"F0.imprint","INTERSECT",VERTEX,{"disambiguationData":[OD(0.0)],"derivedFrom":[subQ1,subQ0]});Q57=makeQuery(id+"F0.imprint","IMPRINT",FACE,{"disambiguationData":[TD([[makeQuery(id+"F0.imprint","IMPRINT",EDGE,{"disambiguationData":[TD([[subQ2,1.0]])],"derivedFrom":subQ1}),1.0]])]});}
            var Q58;
            {var subQ0=sQuery(id+"F0.wireOp",EDGE,"E6.10.5.0");var subQ1=sQuery(id+"F0.wireOp",EDGE,"E6.7.5.0");var subQ2=makeQuery(id+"F0.imprint","INTERSECT",VERTEX,{"disambiguationData":[OD(0.0)],"derivedFrom":[subQ1,subQ0]});Q58=makeQuery(id+"F0.imprint","IMPRINT",FACE,{"disambiguationData":[TD([[makeQuery(id+"F0.imprint","IMPRINT",EDGE,{"disambiguationData":[TD([[subQ2,-1.0]])],"derivedFrom":subQ1}),1.0]])]});}
            var Q59;
            {var subQ0=sQuery(id+"F0.wireOp",EDGE,"E6.10.3.0");var subQ1=sQuery(id+"F0.wireOp",EDGE,"E6.7.3.0");var subQ2=makeQuery(id+"F0.imprint","INTERSECT",VERTEX,{"disambiguationData":[OD(0.0)],"derivedFrom":[subQ1,subQ0]});Q59=makeQuery(id+"F0.imprint","IMPRINT",FACE,{"disambiguationData":[TD([[makeQuery(id+"F0.imprint","IMPRINT",EDGE,{"disambiguationData":[TD([[subQ2,-1.0]])],"derivedFrom":subQ1}),1.0]])]});}
            var Q60;
            {var subQ0=sQuery(id+"F0.wireOp",EDGE,"E7.10.7.0");var subQ1=sQuery(id+"F0.wireOp",EDGE,"E7.7.7.0");var subQ2=makeQuery(id+"F0.imprint","INTERSECT",VERTEX,{"disambiguationData":[OD(0.0)],"derivedFrom":[subQ1,subQ0]});Q60=makeQuery(id+"F0.imprint","IMPRINT",FACE,{"disambiguationData":[TD([[makeQuery(id+"F0.imprint","IMPRINT",EDGE,{"disambiguationData":[TD([[subQ2,-1.0]])],"derivedFrom":subQ1}),1.0]])]});}
            var Q61;
            {var subQ0=sQuery(id+"F0.wireOp",EDGE,"E4");var subQ1=sQuery(id+"F0.wireOp",EDGE,"E1");var subQ2=makeQuery(id+"F0.imprint","INTERSECT",VERTEX,{"disambiguationData":[OD(0.0)],"derivedFrom":[subQ1,subQ0]});Q61=makeQuery(id+"F0.imprint","IMPRINT",FACE,{"disambiguationData":[TD([[makeQuery(id+"F0.imprint","IMPRINT",EDGE,{"disambiguationData":[TD([[subQ2,1.0]])],"derivedFrom":subQ1}),1.0]])]});}
            var Q62;
            {var subQ0=sQuery(id+"F0.wireOp",EDGE,"E5.1.3");var subQ1=sQuery(id+"F0.wireOp",EDGE,"E5.1.2");var subQ2=makeQuery(id+"F0.imprint","INTERSECT",VERTEX,{"disambiguationData":[OD(0.0)],"derivedFrom":[subQ1,subQ0]});Q62=makeQuery(id+"F0.imprint","IMPRINT",FACE,{"disambiguationData":[TD([[makeQuery(id+"F0.imprint","IMPRINT",EDGE,{"disambiguationData":[TD([[subQ2,1.0]])],"derivedFrom":subQ1}),1.0]])]});}
            var Q63;
            {var subQ0=sQuery(id+"F0.wireOp",EDGE,"E7.10.11.0");var subQ1=sQuery(id+"F0.wireOp",EDGE,"E7.7.11.0");var subQ2=makeQuery(id+"F0.imprint","INTERSECT",VERTEX,{"disambiguationData":[OD(0.0)],"derivedFrom":[subQ1,subQ0]});Q63=makeQuery(id+"F0.imprint","IMPRINT",FACE,{"disambiguationData":[TD([[makeQuery(id+"F0.imprint","IMPRINT",EDGE,{"disambiguationData":[TD([[subQ2,-1.0]])],"derivedFrom":subQ1}),1.0]])]});}
            var Q64;
            {var subQ1=sQuery(id+"F0.wireOp",EDGE,"E2");var subQ3=sQuery(id+"F0.wireOp",EDGE,"E5.1.4");var subQ4=makeQuery(id+"F0.imprint","INTERSECT",VERTEX,{"derivedFrom":[subQ1,subQ3]});Q64=makeQuery(id+"F0.imprint","IMPRINT",FACE,{"disambiguationData":[TD([[makeQuery(id+"F0.imprint","IMPRINT",EDGE,{"disambiguationData":[TD([[subQ4,1.0]])],"derivedFrom":subQ3}),1.0]])]});}
            var Q65;
            {var subQ0=sQuery(id+"F0.wireOp",EDGE,"E6.10.6.0");var subQ1=sQuery(id+"F0.wireOp",EDGE,"E6.7.6.0");var subQ2=makeQuery(id+"F0.imprint","INTERSECT",VERTEX,{"disambiguationData":[OD(0.0)],"derivedFrom":[subQ1,subQ0]});Q65=makeQuery(id+"F0.imprint","IMPRINT",FACE,{"disambiguationData":[TD([[makeQuery(id+"F0.imprint","IMPRINT",EDGE,{"disambiguationData":[TD([[subQ2,-1.0]])],"derivedFrom":subQ1}),1.0]])]});}
            var Q66;
            {var subQ0=sQuery(id+"F0.wireOp",EDGE,"E6.10.5.0");var subQ1=sQuery(id+"F0.wireOp",EDGE,"E6.6.5.0");var subQ2=makeQuery(id+"F0.imprint","INTERSECT",VERTEX,{"disambiguationData":[OD(0.0)],"derivedFrom":[subQ1,subQ0]});Q66=makeQuery(id+"F0.imprint","IMPRINT",FACE,{"disambiguationData":[TD([[makeQuery(id+"F0.imprint","IMPRINT",EDGE,{"disambiguationData":[TD([[subQ2,1.0]])],"derivedFrom":subQ1}),1.0]])]});}
            var Q67;
            {var subQ0=sQuery(id+"F0.wireOp",EDGE,"E7.10.9.0");var subQ1=sQuery(id+"F0.wireOp",EDGE,"E7.6.9.0");var subQ2=makeQuery(id+"F0.imprint","INTERSECT",VERTEX,{"disambiguationData":[OD(0.0)],"derivedFrom":[subQ1,subQ0]});Q67=makeQuery(id+"F0.imprint","IMPRINT",FACE,{"disambiguationData":[TD([[makeQuery(id+"F0.imprint","IMPRINT",EDGE,{"disambiguationData":[TD([[subQ2,1.0]])],"derivedFrom":subQ1}),1.0]])]});}
            var Q68;
            {var subQ1=sQuery(id+"F0.wireOp",EDGE,"E3");var subQ3=sQuery(id+"F0.wireOp",EDGE,"E5.1.0");var subQ4=makeQuery(id+"F0.imprint","INTERSECT",VERTEX,{"derivedFrom":[subQ1,subQ3]});Q68=makeQuery(id+"F0.imprint","IMPRINT",FACE,{"disambiguationData":[TD([[makeQuery(id+"F0.imprint","IMPRINT",EDGE,{"disambiguationData":[TD([[subQ4,1.0]])],"derivedFrom":subQ1}),-1.0]])]});}
            var Q69;
            {var subQ1=sQuery(id+"F0.wireOp",EDGE,"E6.6.6.0");var subQ3=sQuery(id+"F0.wireOp",EDGE,"E7.7.7.0");var subQ4=makeQuery(id+"F0.imprint","INTERSECT",VERTEX,{"derivedFrom":[subQ1,subQ3]});Q69=makeQuery(id+"F0.imprint","IMPRINT",FACE,{"disambiguationData":[TD([[makeQuery(id+"F0.imprint","IMPRINT",EDGE,{"disambiguationData":[TD([[subQ4,1.0]])],"derivedFrom":subQ1}),-1.0]])]});}
            var Q70;
            {var subQ1=sQuery(id+"F0.wireOp",EDGE,"E6.12.4.0");var subQ3=sQuery(id+"F0.wireOp",EDGE,"E6.12.5.0");var subQ4=makeQuery(id+"F0.imprint","INTERSECT",VERTEX,{"derivedFrom":[subQ1,subQ3]});Q70=makeQuery(id+"F0.imprint","IMPRINT",FACE,{"disambiguationData":[TD([[makeQuery(id+"F0.imprint","IMPRINT",EDGE,{"disambiguationData":[TD([[subQ4,1.0]])],"derivedFrom":subQ3}),1.0]])]});}
            var Q71;
            {var subQ1=sQuery(id+"F0.wireOp",EDGE,"E7.6.12.0");var subQ3=sQuery(id+"F0.wireOp",EDGE,"E7.7.13.0");var subQ4=makeQuery(id+"F0.imprint","INTERSECT",VERTEX,{"derivedFrom":[subQ1,subQ3]});Q71=makeQuery(id+"F0.imprint","IMPRINT",FACE,{"disambiguationData":[TD([[makeQuery(id+"F0.imprint","IMPRINT",EDGE,{"disambiguationData":[TD([[subQ4,1.0]])],"derivedFrom":subQ1}),-1.0]])]});}
            var Q72;
            {var subQ1=sQuery(id+"F0.wireOp",EDGE,"E5.2.2");var subQ3=sQuery(id+"F0.wireOp",EDGE,"E6.7.3.0");var subQ4=makeQuery(id+"F0.imprint","INTERSECT",VERTEX,{"derivedFrom":[subQ1,subQ3]});Q72=makeQuery(id+"F0.imprint","IMPRINT",FACE,{"disambiguationData":[TD([[makeQuery(id+"F0.imprint","IMPRINT",EDGE,{"disambiguationData":[TD([[subQ4,1.0]])],"derivedFrom":subQ1}),-1.0]])]});}
            var Q73;
            {var subQ1=sQuery(id+"F0.wireOp",EDGE,"E7.12.11.0");var subQ3=sQuery(id+"F0.wireOp",EDGE,"E7.12.12.0");var subQ4=makeQuery(id+"F0.imprint","INTERSECT",VERTEX,{"derivedFrom":[subQ1,subQ3]});Q73=makeQuery(id+"F0.imprint","IMPRINT",FACE,{"disambiguationData":[TD([[makeQuery(id+"F0.imprint","IMPRINT",EDGE,{"disambiguationData":[TD([[subQ4,1.0]])],"derivedFrom":subQ3}),1.0]])]});}
            var Q74;
            {var subQ1=sQuery(id+"F0.wireOp",EDGE,"E5.1.4");var subQ3=sQuery(id+"F0.wireOp",EDGE,"E5.2.4");var subQ4=makeQuery(id+"F0.imprint","INTERSECT",VERTEX,{"derivedFrom":[subQ1,subQ3]});Q74=makeQuery(id+"F0.imprint","IMPRINT",FACE,{"disambiguationData":[TD([[makeQuery(id+"F0.imprint","IMPRINT",EDGE,{"disambiguationData":[TD([[subQ4,1.0]])],"derivedFrom":subQ3}),1.0]])]});}
            var Q75;
            {var subQ1=sQuery(id+"F0.wireOp",EDGE,"E7.6.7.0");var subQ3=sQuery(id+"F0.wireOp",EDGE,"E7.7.8.0");var subQ4=makeQuery(id+"F0.imprint","INTERSECT",VERTEX,{"derivedFrom":[subQ1,subQ3]});Q75=makeQuery(id+"F0.imprint","IMPRINT",FACE,{"disambiguationData":[TD([[makeQuery(id+"F0.imprint","IMPRINT",EDGE,{"disambiguationData":[TD([[subQ4,1.0]])],"derivedFrom":subQ1}),-1.0]])]});}
            var Q76;
            {var subQ1=sQuery(id+"F0.wireOp",EDGE,"E7.6.10.0");var subQ3=sQuery(id+"F0.wireOp",EDGE,"E7.7.11.0");var subQ4=makeQuery(id+"F0.imprint","INTERSECT",VERTEX,{"derivedFrom":[subQ1,subQ3]});Q76=makeQuery(id+"F0.imprint","IMPRINT",FACE,{"disambiguationData":[TD([[makeQuery(id+"F0.imprint","IMPRINT",EDGE,{"disambiguationData":[TD([[subQ4,1.0]])],"derivedFrom":subQ1}),-1.0]])]});}
            var Q77;
            {var subQ1=sQuery(id+"F0.wireOp",EDGE,"E7.6.11.0");var subQ3=sQuery(id+"F0.wireOp",EDGE,"E7.7.12.0");var subQ4=makeQuery(id+"F0.imprint","INTERSECT",VERTEX,{"derivedFrom":[subQ1,subQ3]});Q77=makeQuery(id+"F0.imprint","IMPRINT",FACE,{"disambiguationData":[TD([[makeQuery(id+"F0.imprint","IMPRINT",EDGE,{"disambiguationData":[TD([[subQ4,1.0]])],"derivedFrom":subQ1}),-1.0]])]});}
            var Q78;
            {var subQ1=sQuery(id+"F0.wireOp",EDGE,"E5.2.4");var subQ3=sQuery(id+"F0.wireOp",EDGE,"E6.12.3.0");var subQ4=makeQuery(id+"F0.imprint","INTERSECT",VERTEX,{"derivedFrom":[subQ1,subQ3]});Q78=makeQuery(id+"F0.imprint","IMPRINT",FACE,{"disambiguationData":[TD([[makeQuery(id+"F0.imprint","IMPRINT",EDGE,{"disambiguationData":[TD([[subQ4,1.0]])],"derivedFrom":subQ3}),1.0]])]});}
            var Q79;
            {var subQ1=sQuery(id+"F0.wireOp",EDGE,"E4");var subQ3=sQuery(id+"F0.wireOp",EDGE,"E7.6.14.0");var subQ4=makeQuery(id+"F0.imprint","INTERSECT",VERTEX,{"derivedFrom":[subQ1,subQ3]});Q79=makeQuery(id+"F0.imprint","IMPRINT",FACE,{"disambiguationData":[TD([[makeQuery(id+"F0.imprint","IMPRINT",EDGE,{"disambiguationData":[TD([[subQ4,-1.0]])],"derivedFrom":subQ1}),-1.0]])]});}
            var Q80;
            {var subQ1=sQuery(id+"F0.wireOp",EDGE,"E7.12.12.0");var subQ3=sQuery(id+"F0.wireOp",EDGE,"E7.12.13.0");var subQ4=makeQuery(id+"F0.imprint","INTERSECT",VERTEX,{"derivedFrom":[subQ1,subQ3]});Q80=makeQuery(id+"F0.imprint","IMPRINT",FACE,{"disambiguationData":[TD([[makeQuery(id+"F0.imprint","IMPRINT",EDGE,{"disambiguationData":[TD([[subQ4,1.0]])],"derivedFrom":subQ3}),1.0]])]});}
            var Q81;
            {var subQ1=sQuery(id+"F0.wireOp",EDGE,"E6.6.4.0");var subQ3=sQuery(id+"F0.wireOp",EDGE,"E6.7.5.0");var subQ4=makeQuery(id+"F0.imprint","INTERSECT",VERTEX,{"derivedFrom":[subQ1,subQ3]});Q81=makeQuery(id+"F0.imprint","IMPRINT",FACE,{"disambiguationData":[TD([[makeQuery(id+"F0.imprint","IMPRINT",EDGE,{"disambiguationData":[TD([[subQ4,1.0]])],"derivedFrom":subQ1}),-1.0]])]});}
            var Q82;
            {var subQ1=sQuery(id+"F0.wireOp",EDGE,"E7.12.9.0");var subQ3=sQuery(id+"F0.wireOp",EDGE,"E7.12.10.0");var subQ4=makeQuery(id+"F0.imprint","INTERSECT",VERTEX,{"derivedFrom":[subQ1,subQ3]});Q82=makeQuery(id+"F0.imprint","IMPRINT",FACE,{"disambiguationData":[TD([[makeQuery(id+"F0.imprint","IMPRINT",EDGE,{"disambiguationData":[TD([[subQ4,1.0]])],"derivedFrom":subQ3}),1.0]])]});}
            var Q83;
            {var subQ1=sQuery(id+"F0.wireOp",EDGE,"E7.6.8.0");var subQ3=sQuery(id+"F0.wireOp",EDGE,"E7.7.9.0");var subQ4=makeQuery(id+"F0.imprint","INTERSECT",VERTEX,{"derivedFrom":[subQ1,subQ3]});Q83=makeQuery(id+"F0.imprint","IMPRINT",FACE,{"disambiguationData":[TD([[makeQuery(id+"F0.imprint","IMPRINT",EDGE,{"disambiguationData":[TD([[subQ4,1.0]])],"derivedFrom":subQ1}),-1.0]])]});}
            var Q84;
            {var subQ1=sQuery(id+"F0.wireOp",EDGE,"E6.6.3.0");var subQ3=sQuery(id+"F0.wireOp",EDGE,"E6.7.4.0");var subQ4=makeQuery(id+"F0.imprint","INTERSECT",VERTEX,{"derivedFrom":[subQ1,subQ3]});Q84=makeQuery(id+"F0.imprint","IMPRINT",FACE,{"disambiguationData":[TD([[makeQuery(id+"F0.imprint","IMPRINT",EDGE,{"disambiguationData":[TD([[subQ4,1.0]])],"derivedFrom":subQ1}),-1.0]])]});}
            var Q85;
            {var subQ1=sQuery(id+"F0.wireOp",EDGE,"E6.12.6.0");var subQ3=sQuery(id+"F0.wireOp",EDGE,"E7.12.7.0");var subQ4=makeQuery(id+"F0.imprint","INTERSECT",VERTEX,{"derivedFrom":[subQ1,subQ3]});Q85=makeQuery(id+"F0.imprint","IMPRINT",FACE,{"disambiguationData":[TD([[makeQuery(id+"F0.imprint","IMPRINT",EDGE,{"disambiguationData":[TD([[subQ4,1.0]])],"derivedFrom":subQ1}),1.0]])]});}
            var Q86;
            {var subQ1=sQuery(id+"F0.wireOp",EDGE,"E2");var subQ3=sQuery(id+"F0.wireOp",EDGE,"E7.12.14.0");var subQ4=makeQuery(id+"F0.imprint","INTERSECT",VERTEX,{"derivedFrom":[subQ1,subQ3]});Q86=makeQuery(id+"F0.imprint","IMPRINT",FACE,{"disambiguationData":[TD([[makeQuery(id+"F0.imprint","IMPRINT",EDGE,{"disambiguationData":[TD([[subQ4,-1.0]])],"derivedFrom":subQ1}),1.0]])]});}
            var Q87;
            {var subQ1=sQuery(id+"F0.wireOp",EDGE,"E6.12.4.0");var subQ3=sQuery(id+"F0.wireOp",EDGE,"E6.12.5.0");var subQ4=makeQuery(id+"F0.imprint","INTERSECT",VERTEX,{"derivedFrom":[subQ1,subQ3]});Q87=makeQuery(id+"F0.imprint","IMPRINT",FACE,{"disambiguationData":[TD([[makeQuery(id+"F0.imprint","IMPRINT",EDGE,{"disambiguationData":[TD([[subQ4,1.0]])],"derivedFrom":subQ1}),1.0]])]});}
            var Q88;
            {var subQ1=sQuery(id+"F0.wireOp",EDGE,"E7.12.8.0");var subQ3=sQuery(id+"F0.wireOp",EDGE,"E7.12.9.0");var subQ4=makeQuery(id+"F0.imprint","INTERSECT",VERTEX,{"derivedFrom":[subQ1,subQ3]});Q88=makeQuery(id+"F0.imprint","IMPRINT",FACE,{"disambiguationData":[TD([[makeQuery(id+"F0.imprint","IMPRINT",EDGE,{"disambiguationData":[TD([[subQ4,1.0]])],"derivedFrom":subQ1}),1.0]])]});}
            var Q89;
            {var subQ1=sQuery(id+"F0.wireOp",EDGE,"E7.6.13.0");var subQ3=sQuery(id+"F0.wireOp",EDGE,"E7.7.14.0");var subQ4=makeQuery(id+"F0.imprint","INTERSECT",VERTEX,{"derivedFrom":[subQ1,subQ3]});Q89=makeQuery(id+"F0.imprint","IMPRINT",FACE,{"disambiguationData":[TD([[makeQuery(id+"F0.imprint","IMPRINT",EDGE,{"disambiguationData":[TD([[subQ4,1.0]])],"derivedFrom":subQ1}),-1.0]])]});}
            var Q90;
            {var subQ1=sQuery(id+"F0.wireOp",EDGE,"E7.12.9.0");var subQ3=sQuery(id+"F0.wireOp",EDGE,"E7.12.10.0");var subQ4=makeQuery(id+"F0.imprint","INTERSECT",VERTEX,{"derivedFrom":[subQ1,subQ3]});Q90=makeQuery(id+"F0.imprint","IMPRINT",FACE,{"disambiguationData":[TD([[makeQuery(id+"F0.imprint","IMPRINT",EDGE,{"disambiguationData":[TD([[subQ4,1.0]])],"derivedFrom":subQ1}),1.0]])]});}
            var Q91;
            {var subQ1=sQuery(id+"F0.wireOp",EDGE,"E6.6.5.0");var subQ3=sQuery(id+"F0.wireOp",EDGE,"E6.7.6.0");var subQ4=makeQuery(id+"F0.imprint","INTERSECT",VERTEX,{"derivedFrom":[subQ1,subQ3]});Q91=makeQuery(id+"F0.imprint","IMPRINT",FACE,{"disambiguationData":[TD([[makeQuery(id+"F0.imprint","IMPRINT",EDGE,{"disambiguationData":[TD([[subQ4,1.0]])],"derivedFrom":subQ1}),-1.0]])]});}
            var Q92;
            {var subQ1=sQuery(id+"F0.wireOp",EDGE,"E7.12.11.0");var subQ3=sQuery(id+"F0.wireOp",EDGE,"E7.12.12.0");var subQ4=makeQuery(id+"F0.imprint","INTERSECT",VERTEX,{"derivedFrom":[subQ1,subQ3]});Q92=makeQuery(id+"F0.imprint","IMPRINT",FACE,{"disambiguationData":[TD([[makeQuery(id+"F0.imprint","IMPRINT",EDGE,{"disambiguationData":[TD([[subQ4,1.0]])],"derivedFrom":subQ1}),1.0]])]});}
            var Q93;
            {var subQ0=sQuery(id+"F0.wireOp",EDGE,"E5.1.4");var subQ1=sQuery(id+"F0.wireOp",EDGE,"E2");var subQ2=makeQuery(id+"F0.imprint","INTERSECT",VERTEX,{"derivedFrom":[subQ1,subQ0]});Q93=makeQuery(id+"F0.imprint","IMPRINT",FACE,{"disambiguationData":[TD([[makeQuery(id+"F0.imprint","IMPRINT",EDGE,{"disambiguationData":[TD([[subQ2,-1.0]])],"derivedFrom":subQ1}),1.0]])]});}
            var Q94;
            {var subQ1=sQuery(id+"F0.wireOp",EDGE,"E2");var subQ3=sQuery(id+"F0.wireOp",EDGE,"E5.1.4");var subQ4=makeQuery(id+"F0.imprint","INTERSECT",VERTEX,{"derivedFrom":[subQ1,subQ3]});Q94=makeQuery(id+"F0.imprint","IMPRINT",FACE,{"disambiguationData":[TD([[makeQuery(id+"F0.imprint","IMPRINT",EDGE,{"disambiguationData":[TD([[subQ4,1.0]])],"derivedFrom":subQ1}),1.0]])]});}
            var Q95;
            {var subQ1=sQuery(id+"F0.wireOp",EDGE,"E6.12.3.0");var subQ3=sQuery(id+"F0.wireOp",EDGE,"E6.12.4.0");var subQ4=makeQuery(id+"F0.imprint","INTERSECT",VERTEX,{"derivedFrom":[subQ1,subQ3]});Q95=makeQuery(id+"F0.imprint","IMPRINT",FACE,{"disambiguationData":[TD([[makeQuery(id+"F0.imprint","IMPRINT",EDGE,{"disambiguationData":[TD([[subQ4,1.0]])],"derivedFrom":subQ1}),1.0]])]});}
            var Q96;
            {var subQ1=sQuery(id+"F0.wireOp",EDGE,"E7.12.10.0");var subQ3=sQuery(id+"F0.wireOp",EDGE,"E7.12.11.0");var subQ4=makeQuery(id+"F0.imprint","INTERSECT",VERTEX,{"derivedFrom":[subQ1,subQ3]});Q96=makeQuery(id+"F0.imprint","IMPRINT",FACE,{"disambiguationData":[TD([[makeQuery(id+"F0.imprint","IMPRINT",EDGE,{"disambiguationData":[TD([[subQ4,1.0]])],"derivedFrom":subQ1}),1.0]])]});}
            var Q97;
            {var subQ1=sQuery(id+"F0.wireOp",EDGE,"E7.12.12.0");var subQ3=sQuery(id+"F0.wireOp",EDGE,"E7.12.13.0");var subQ4=makeQuery(id+"F0.imprint","INTERSECT",VERTEX,{"derivedFrom":[subQ1,subQ3]});Q97=makeQuery(id+"F0.imprint","IMPRINT",FACE,{"disambiguationData":[TD([[makeQuery(id+"F0.imprint","IMPRINT",EDGE,{"disambiguationData":[TD([[subQ4,1.0]])],"derivedFrom":subQ1}),1.0]])]});}
            var Q98;
            {var subQ1=sQuery(id+"F0.wireOp",EDGE,"E7.6.9.0");var subQ3=sQuery(id+"F0.wireOp",EDGE,"E7.7.10.0");var subQ4=makeQuery(id+"F0.imprint","INTERSECT",VERTEX,{"derivedFrom":[subQ1,subQ3]});Q98=makeQuery(id+"F0.imprint","IMPRINT",FACE,{"disambiguationData":[TD([[makeQuery(id+"F0.imprint","IMPRINT",EDGE,{"disambiguationData":[TD([[subQ4,1.0]])],"derivedFrom":subQ1}),-1.0]])]});}
            var Q99;
            {var subQ1=sQuery(id+"F0.wireOp",EDGE,"E5.1.2");var subQ3=sQuery(id+"F0.wireOp",EDGE,"E5.2.0");var subQ4=makeQuery(id+"F0.imprint","INTERSECT",VERTEX,{"derivedFrom":[subQ1,subQ3]});Q99=makeQuery(id+"F0.imprint","IMPRINT",FACE,{"disambiguationData":[TD([[makeQuery(id+"F0.imprint","IMPRINT",EDGE,{"disambiguationData":[TD([[subQ4,1.0]])],"derivedFrom":subQ1}),-1.0]])]});}
            var Q100;
            {var subQ1=sQuery(id+"F0.wireOp",EDGE,"E7.12.7.0");var subQ3=sQuery(id+"F0.wireOp",EDGE,"E7.12.8.0");var subQ4=makeQuery(id+"F0.imprint","INTERSECT",VERTEX,{"derivedFrom":[subQ1,subQ3]});Q100=makeQuery(id+"F0.imprint","IMPRINT",FACE,{"disambiguationData":[TD([[makeQuery(id+"F0.imprint","IMPRINT",EDGE,{"disambiguationData":[TD([[subQ4,1.0]])],"derivedFrom":subQ1}),1.0]])]});}
            var Q101;
            {var subQ1=sQuery(id+"F0.wireOp",EDGE,"E6.12.3.0");var subQ3=sQuery(id+"F0.wireOp",EDGE,"E6.12.4.0");var subQ4=makeQuery(id+"F0.imprint","INTERSECT",VERTEX,{"derivedFrom":[subQ1,subQ3]});Q101=makeQuery(id+"F0.imprint","IMPRINT",FACE,{"disambiguationData":[TD([[makeQuery(id+"F0.imprint","IMPRINT",EDGE,{"disambiguationData":[TD([[subQ4,1.0]])],"derivedFrom":subQ3}),1.0]])]});}
            var Q102;
            {var subQ1=sQuery(id+"F0.wireOp",EDGE,"E5.2.4");var subQ3=sQuery(id+"F0.wireOp",EDGE,"E6.12.3.0");var subQ4=makeQuery(id+"F0.imprint","INTERSECT",VERTEX,{"derivedFrom":[subQ1,subQ3]});Q102=makeQuery(id+"F0.imprint","IMPRINT",FACE,{"disambiguationData":[TD([[makeQuery(id+"F0.imprint","IMPRINT",EDGE,{"disambiguationData":[TD([[subQ4,1.0]])],"derivedFrom":subQ1}),1.0]])]});}
            var Q103;
            {var subQ1=sQuery(id+"F0.wireOp",EDGE,"E6.12.5.0");var subQ3=sQuery(id+"F0.wireOp",EDGE,"E6.12.6.0");var subQ4=makeQuery(id+"F0.imprint","INTERSECT",VERTEX,{"derivedFrom":[subQ1,subQ3]});Q103=makeQuery(id+"F0.imprint","IMPRINT",FACE,{"disambiguationData":[TD([[makeQuery(id+"F0.imprint","IMPRINT",EDGE,{"disambiguationData":[TD([[subQ4,1.0]])],"derivedFrom":subQ1}),1.0]])]});}
            var Q104;
            {var subQ1=sQuery(id+"F0.wireOp",EDGE,"E5.1.4");var subQ3=sQuery(id+"F0.wireOp",EDGE,"E5.2.4");var subQ4=makeQuery(id+"F0.imprint","INTERSECT",VERTEX,{"derivedFrom":[subQ1,subQ3]});Q104=makeQuery(id+"F0.imprint","IMPRINT",FACE,{"disambiguationData":[TD([[makeQuery(id+"F0.imprint","IMPRINT",EDGE,{"disambiguationData":[TD([[subQ4,1.0]])],"derivedFrom":subQ1}),1.0]])]});}
            var Q105;
            {var subQ1=sQuery(id+"F0.wireOp",EDGE,"E7.12.13.0");var subQ3=sQuery(id+"F0.wireOp",EDGE,"E7.12.14.0");var subQ4=makeQuery(id+"F0.imprint","INTERSECT",VERTEX,{"derivedFrom":[subQ1,subQ3]});Q105=makeQuery(id+"F0.imprint","IMPRINT",FACE,{"disambiguationData":[TD([[makeQuery(id+"F0.imprint","IMPRINT",EDGE,{"disambiguationData":[TD([[subQ4,1.0]])],"derivedFrom":subQ1}),1.0]])]});}
            extrude(context, id + "F1", {"entities" : qUnion([Q0, Q1, Q2, Q3, Q4, Q5, Q6, Q7, Q8, Q9, Q10, Q11, Q12, Q13, Q14, Q15, Q16, Q17, Q18, Q19, Q20, Q21, Q22, Q23, Q24, Q25, Q26, Q27, Q28, Q29, Q30, Q31, Q32, Q33, Q34, Q35, Q36, Q37, Q38, Q39, Q40, Q41, Q42, Q43, Q44, Q45, Q46, Q47, Q48, Q49, Q50, Q51, Q52, Q53, Q54, Q55, Q56, Q57, Q58, Q59, Q60, Q61, Q62, Q63, Q64, Q65, Q66, Q67, Q68, Q69, Q70, Q71, Q72, Q73, Q74, Q75, Q76, Q77, Q78, Q79, Q80, Q81, Q82, Q83, Q84, Q85, Q86, Q87, Q88, Q89, Q90, Q91, Q92, Q93, Q94, Q95, Q96, Q97, Q98, Q99, Q100, Q101, Q102, Q103, Q104, Q105]), "depth" : 5 * mm, "offsetDistance" : 25 * mm});
        }
        {
            var Q0;
            Q0=makeQuery(id+"F1.opExtrude","CAP_FACE",FACE,{"disambiguationData":[OSD([sQuery(id+"F0.wireOp",EDGE,"E1"),sQuery(id+"F0.wireOp",EDGE,"E3"),sQuery(id+"F0.wireOp",EDGE,"E4"),sQuery(id+"F0.wireOp",EDGE,"E5.1.0"),sQuery(id+"F0.wireOp",EDGE,"E5.1.2"),sQuery(id+"F0.wireOp",EDGE,"E5.1.3"),sQuery(id+"F0.wireOp",EDGE,"E5.2.0"),sQuery(id+"F0.wireOp",EDGE,"E5.2.2"),sQuery(id+"F0.wireOp",EDGE,"E5.2.3"),sQuery(id+"F0.wireOp",EDGE,"E5.3.0"),sQuery(id+"F0.wireOp",EDGE,"E5.3.2"),sQuery(id+"F0.wireOp",EDGE,"E5.3.3"),sQuery(id+"F0.wireOp",EDGE,"E5.4.0"),sQuery(id+"F0.wireOp",EDGE,"E5.4.2"),sQuery(id+"F0.wireOp",EDGE,"E5.4.3"),sQuery(id+"F0.wireOp",EDGE,"E5.5.0"),sQuery(id+"F0.wireOp",EDGE,"E5.5.2"),sQuery(id+"F0.wireOp",EDGE,"E5.5.3"),sQuery(id+"F0.wireOp",EDGE,"E5.6.0"),sQuery(id+"F0.wireOp",EDGE,"E5.6.1"),sQuery(id+"F0.wireOp",EDGE,"E5.6.2"),sQuery(id+"F0.wireOp",EDGE,"E5.6.3")])],"isStart":false});
            var sketch = newSketch(context, id + "F2", { "sketchPlane" : qUnion([Q0])});
            skCircle(sketch, "E8", {"center": v(0, 0) * mm, "radius": 11.07 * mm});
            skCircle(sketch, "E9", {"center": v(0, 27.13) * mm, "radius": 2.33 * mm});
            skCircle(sketch, "E10.1.0", {"center": v(-11.04, 24.79) * mm, "radius": 2.33 * mm});
            skCircle(sketch, "E10.2.0", {"center": v(-20.16, 18.16) * mm, "radius": 2.32 * mm});
            skCircle(sketch, "E10.3.0", {"center": v(-25.8, 8.39) * mm, "radius": 2.33 * mm});
            skCircle(sketch, "E10.4.0", {"center": v(-26.99, -2.84) * mm, "radius": 2.33 * mm});
            skCircle(sketch, "E10.5.0", {"center": v(-23.5, -13.57) * mm, "radius": 2.33 * mm});
            skCircle(sketch, "E10.6.0", {"center": v(-15.95, -21.95) * mm, "radius": 2.33 * mm});
            skCircle(sketch, "E11.1.7.0", {"center": v(-5.64, -26.54) * mm, "radius": 2.33 * mm});
            skCircle(sketch, "E11.1.8.0", {"center": v(5.64, -26.54) * mm, "radius": 2.33 * mm});
            skCircle(sketch, "E11.1.9.0", {"center": v(15.95, -21.95) * mm, "radius": 2.33 * mm});
            skCircle(sketch, "E11.1.10.0", {"center": v(23.5, -13.57) * mm, "radius": 2.33 * mm});
            skCircle(sketch, "E12.1.11.0", {"center": v(26.99, -2.84) * mm, "radius": 2.33 * mm});
            skCircle(sketch, "E12.1.12.0", {"center": v(25.8, 8.39) * mm, "radius": 2.33 * mm});
            skCircle(sketch, "E12.1.13.0", {"center": v(20.16, 18.16) * mm, "radius": 2.33 * mm});
            skCircle(sketch, "E12.1.14.0", {"center": v(11.04, 24.79) * mm, "radius": 2.33 * mm});
            skSolve(sketch);
        }
        {
            var Q0;
            Q0 = qSketchRegion(id + "F2", true);
            extrude(context, id + "F3", {"entities" : qUnion([Q0]), "operationType" : NewBodyOperationType.REMOVE, "endBound" : BoundingType.THROUGH_ALL, "oppositeDirection" : true, "depth" : 5 * mm, "offsetDistance" : 25 * mm});
        }
    });
